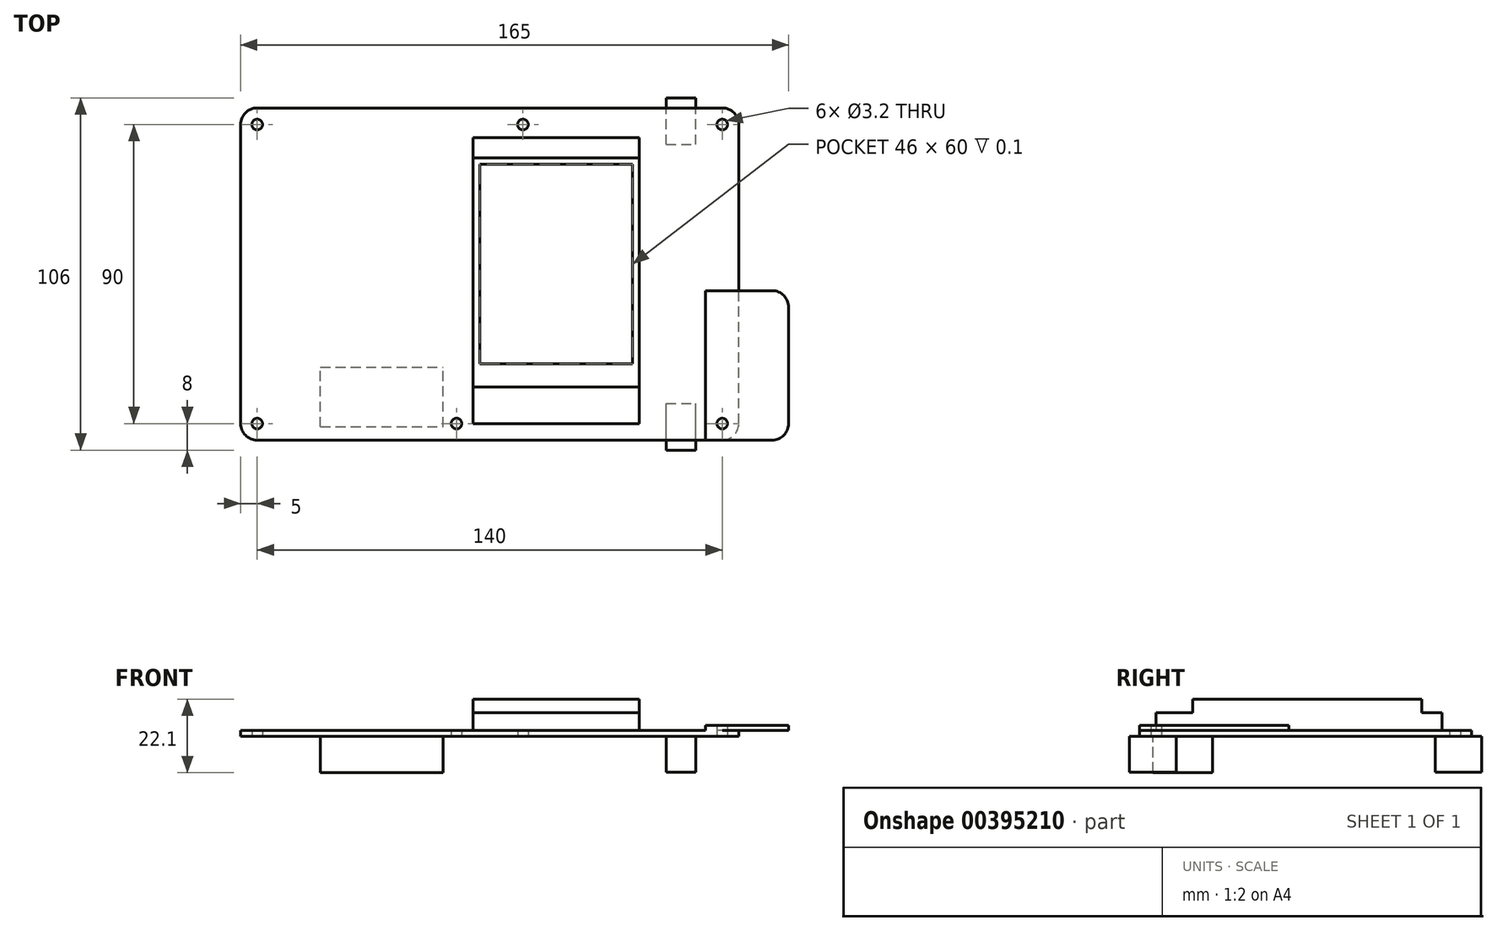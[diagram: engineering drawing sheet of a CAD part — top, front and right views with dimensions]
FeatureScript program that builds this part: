
annotation { "Feature Type Name" : "Feature", "Feature Type Description" : "" }
export const myFeature = defineFeature(function(context is Context, id is Id, definition is map)
    precondition{}
    {
        {
            var Q0;
            Q0=qCreatedBy(makeId("Top.planeOp"),FACE);
            var sketch = newSketch(context, id + "F0", { "sketchPlane" : qUnion([Q0])});
            skLineSegment(sketch, "E0.bottom", {"start": v(5, 0) * mm, "end": v(145, 0) * mm});
            skLineSegment(sketch, "E0.top", {"start": v(5, 100) * mm, "end": v(145, 100) * mm});
            skLineSegment(sketch, "E0.left", {"start": v(0, 5) * mm, "end": v(0, 95) * mm});
            skLineSegment(sketch, "E0.right", {"start": v(150, 5) * mm, "end": v(150, 95) * mm});
            skPoint(sketch, "E1.visualSharp", {"position": v(0, 100) * mm});
            skArc(sketch, "E1.filletArc", {"start": v(5, 100) * mm, "mid": v(1.46, 98.54) * mm, "end": v(0, 95) * mm});
            skPoint(sketch, "E2.visualSharp", {"position": v(150, 100) * mm});
            skArc(sketch, "E2.filletArc", {"start": v(150, 95) * mm, "mid": v(148.54, 98.54) * mm, "end": v(145, 100) * mm});
            skPoint(sketch, "E3.visualSharp", {"position": v(150, 0) * mm});
            skArc(sketch, "E3.filletArc", {"start": v(145, 0) * mm, "mid": v(148.54, 1.46) * mm, "end": v(150, 5) * mm});
            skPoint(sketch, "E4.visualSharp", {"position": v(0, 0) * mm});
            skArc(sketch, "E4.filletArc", {"start": v(0, 5) * mm, "mid": v(1.46, 1.46) * mm, "end": v(5, 0) * mm});
            skCircle(sketch, "E5", {"center": v(5, 95) * mm, "radius": 1.6 * mm});
            skCircle(sketch, "E6", {"center": v(5, 5) * mm, "radius": 1.6 * mm});
            skCircle(sketch, "E7", {"center": v(145, 5) * mm, "radius": 1.6 * mm});
            skCircle(sketch, "E8", {"center": v(145, 95) * mm, "radius": 1.6 * mm});
            skCircle(sketch, "E9", {"center": v(65, 5) * mm, "radius": 1.6 * mm});
            skCircle(sketch, "E10", {"center": v(85, 95) * mm, "radius": 1.6 * mm});
            skSolve(sketch);
        }
        {
            var Q0;
            Q0 = qSketchRegion(id + "F0", true);
            extrude(context, id + "F1", {"entities" : qUnion([Q0]), "depth" : 1.7 * mm});
        }
        {
            var Q0;
            Q0=makeQuery(id+"F1.opExtrude","CAP_FACE",FACE,{"disambiguationData":[OSD([sQuery(id+"F0.wireOp",EDGE,"E0.bottom"),sQuery(id+"F0.wireOp",EDGE,"E0.top"),sQuery(id+"F0.wireOp",EDGE,"E0.left"),sQuery(id+"F0.wireOp",EDGE,"E0.right"),sQuery(id+"F0.wireOp",EDGE,"E1.filletArc"),sQuery(id+"F0.wireOp",EDGE,"E2.filletArc"),sQuery(id+"F0.wireOp",EDGE,"E3.filletArc"),sQuery(id+"F0.wireOp",EDGE,"E4.filletArc"),sQuery(id+"F0.wireOp",EDGE,"E5"),sQuery(id+"F0.wireOp",EDGE,"E6"),sQuery(id+"F0.wireOp",EDGE,"E7"),sQuery(id+"F0.wireOp",EDGE,"E8"),sQuery(id+"F0.wireOp",EDGE,"E9"),sQuery(id+"F0.wireOp",EDGE,"E10")])],"isStart":false});
            var sketch = newSketch(context, id + "F2", { "sketchPlane" : qUnion([Q0])});
            skLineSegment(sketch, "E11.bottom", {"start": v(70, 91) * mm, "end": v(120, 91) * mm});
            skLineSegment(sketch, "E11.top", {"start": v(70, 5) * mm, "end": v(120, 5) * mm});
            skLineSegment(sketch, "E11.left", {"start": v(70, 91) * mm, "end": v(70, 5) * mm});
            skLineSegment(sketch, "E11.right", {"start": v(120, 91) * mm, "end": v(120, 5) * mm});
            skSolve(sketch);
        }
        {
            var Q0;
            Q0 = qSketchRegion(id + "F2", true);
            extrude(context, id + "F3", {"entities" : qUnion([Q0]), "operationType" : NewBodyOperationType.ADD, "depth" : 5.4 * mm});
        }
        {
            var Q0;
            Q0=makeQuery(id+"F3.opExtrude","CAP_FACE",FACE,{"disambiguationData":[OSD([sQuery(id+"F2.wireOp",EDGE,"E11.bottom"),sQuery(id+"F2.wireOp",EDGE,"E11.top"),sQuery(id+"F2.wireOp",EDGE,"E11.left"),sQuery(id+"F2.wireOp",EDGE,"E11.right")])],"isStart":false});
            var sketch = newSketch(context, id + "F4", { "sketchPlane" : qUnion([Q0])});
            skLineSegment(sketch, "E12.bottom", {"start": v(70, 85) * mm, "end": v(120, 85) * mm});
            skLineSegment(sketch, "E12.top", {"start": v(70, 16) * mm, "end": v(120, 16) * mm});
            skLineSegment(sketch, "E12.left", {"start": v(70, 85) * mm, "end": v(70, 16) * mm});
            skLineSegment(sketch, "E12.right", {"start": v(120, 85) * mm, "end": v(120, 16) * mm});
            skSolve(sketch);
        }
        {
            var Q0;
            Q0 = qSketchRegion(id + "F4", true);
            extrude(context, id + "F5", {"entities" : qUnion([Q0]), "operationType" : NewBodyOperationType.ADD, "depth" : 4 * mm});
        }
        {
            var Q0;
            Q0=makeQuery(id+"F5.opExtrude","CAP_FACE",FACE,{"disambiguationData":[OSD([sQuery(id+"F4.wireOp",EDGE,"E12.bottom"),sQuery(id+"F4.wireOp",EDGE,"E12.top"),sQuery(id+"F4.wireOp",EDGE,"E12.left"),sQuery(id+"F4.wireOp",EDGE,"E12.right")])],"isStart":false});
            var sketch = newSketch(context, id + "F6", { "sketchPlane" : qUnion([Q0])});
            skLineSegment(sketch, "E13.bottom", {"start": v(72, 83) * mm, "end": v(118, 83) * mm});
            skLineSegment(sketch, "E13.top", {"start": v(72, 23) * mm, "end": v(118, 23) * mm});
            skLineSegment(sketch, "E13.left", {"start": v(72, 83) * mm, "end": v(72, 23) * mm});
            skLineSegment(sketch, "E13.right", {"start": v(118, 83) * mm, "end": v(118, 23) * mm});
            skSolve(sketch);
        }
        {
            var Q0;
            Q0 = qSketchRegion(id + "F6", true);
            extrude(context, id + "F7", {"entities" : qUnion([Q0]), "operationType" : NewBodyOperationType.REMOVE, "oppositeDirection" : true, "depth" : .1 * mm});
        }
        {
            var Q0;
            Q0=makeQuery(id+"F1.opExtrude","CAP_FACE",FACE,{"disambiguationData":[OSD([sQuery(id+"F0.wireOp",EDGE,"E0.bottom"),sQuery(id+"F0.wireOp",EDGE,"E0.top"),sQuery(id+"F0.wireOp",EDGE,"E0.left"),sQuery(id+"F0.wireOp",EDGE,"E0.right"),sQuery(id+"F0.wireOp",EDGE,"E1.filletArc"),sQuery(id+"F0.wireOp",EDGE,"E2.filletArc"),sQuery(id+"F0.wireOp",EDGE,"E3.filletArc"),sQuery(id+"F0.wireOp",EDGE,"E4.filletArc"),sQuery(id+"F0.wireOp",EDGE,"E5"),sQuery(id+"F0.wireOp",EDGE,"E6"),sQuery(id+"F0.wireOp",EDGE,"E7"),sQuery(id+"F0.wireOp",EDGE,"E8"),sQuery(id+"F0.wireOp",EDGE,"E9"),sQuery(id+"F0.wireOp",EDGE,"E10")])],"isStart":false});
            var sketch = newSketch(context, id + "F8", { "sketchPlane" : qUnion([Q0])});
            skLineSegment(sketch, "E14.bottom", {"start": v(140, 0) * mm, "end": v(160, 0) * mm});
            skLineSegment(sketch, "E14.top", {"start": v(140, 45) * mm, "end": v(160, 45) * mm});
            skLineSegment(sketch, "E14.left", {"start": v(140, 0) * mm, "end": v(140, 45) * mm});
            skLineSegment(sketch, "E14.right", {"start": v(165, 5) * mm, "end": v(165, 40) * mm});
            skPoint(sketch, "E15.visualSharp", {"position": v(165, 45) * mm});
            skArc(sketch, "E15.filletArc", {"start": v(165, 40) * mm, "mid": v(163.54, 43.54) * mm, "end": v(160, 45) * mm});
            skPoint(sketch, "E16.visualSharp", {"position": v(165, 0) * mm});
            skArc(sketch, "E16.filletArc", {"start": v(160, 0) * mm, "mid": v(163.54, 1.46) * mm, "end": v(165, 5) * mm});
            skCircle(sketch, "E17.0", {"center": v(145, 5) * mm, "radius": 1.6 * mm});
            skSolve(sketch);
        }
        {
            var Q0;
            Q0 = qSketchRegion(id + "F8", true);
            extrude(context, id + "F9", {"entities" : qUnion([Q0]), "operationType" : NewBodyOperationType.ADD, "depth" : 1.6 * mm});
        }
        {
            var Q0;
            Q0=makeQuery(id+"F1.opExtrude","CAP_FACE",FACE,{"disambiguationData":[OSD([sQuery(id+"F0.wireOp",EDGE,"E0.bottom"),sQuery(id+"F0.wireOp",EDGE,"E0.top"),sQuery(id+"F0.wireOp",EDGE,"E0.left"),sQuery(id+"F0.wireOp",EDGE,"E0.right"),sQuery(id+"F0.wireOp",EDGE,"E1.filletArc"),sQuery(id+"F0.wireOp",EDGE,"E2.filletArc"),sQuery(id+"F0.wireOp",EDGE,"E3.filletArc"),sQuery(id+"F0.wireOp",EDGE,"E4.filletArc"),sQuery(id+"F0.wireOp",EDGE,"E5"),sQuery(id+"F0.wireOp",EDGE,"E6"),sQuery(id+"F0.wireOp",EDGE,"E7"),sQuery(id+"F0.wireOp",EDGE,"E8"),sQuery(id+"F0.wireOp",EDGE,"E9"),sQuery(id+"F0.wireOp",EDGE,"E10")])],"isStart":true});
            var sketch = newSketch(context, id + "F10", { "sketchPlane" : qUnion([Q0])});
            skLineSegment(sketch, "E18.bottom", {"start": v(24, -4) * mm, "end": v(61, -4) * mm});
            skLineSegment(sketch, "E18.top", {"start": v(24, -22) * mm, "end": v(61, -22) * mm});
            skLineSegment(sketch, "E18.left", {"start": v(24, -4) * mm, "end": v(24, -22) * mm});
            skLineSegment(sketch, "E18.right", {"start": v(61, -4) * mm, "end": v(61, -22) * mm});
            skSolve(sketch);
        }
        {
            var Q0;
            Q0 = qSketchRegion(id + "F10", true);
            extrude(context, id + "F11", {"entities" : qUnion([Q0]), "operationType" : NewBodyOperationType.ADD, "depth" : 11 * mm});
        }
        {
            var Q0;
            Q0=makeQuery(id+"F1.opExtrude","CAP_FACE",FACE,{"disambiguationData":[OSD([sQuery(id+"F0.wireOp",EDGE,"E0.bottom"),sQuery(id+"F0.wireOp",EDGE,"E0.top"),sQuery(id+"F0.wireOp",EDGE,"E0.left"),sQuery(id+"F0.wireOp",EDGE,"E0.right"),sQuery(id+"F0.wireOp",EDGE,"E1.filletArc"),sQuery(id+"F0.wireOp",EDGE,"E2.filletArc"),sQuery(id+"F0.wireOp",EDGE,"E3.filletArc"),sQuery(id+"F0.wireOp",EDGE,"E4.filletArc"),sQuery(id+"F0.wireOp",EDGE,"E5"),sQuery(id+"F0.wireOp",EDGE,"E6"),sQuery(id+"F0.wireOp",EDGE,"E7"),sQuery(id+"F0.wireOp",EDGE,"E8"),sQuery(id+"F0.wireOp",EDGE,"E9"),sQuery(id+"F0.wireOp",EDGE,"E10")])],"isStart":true});
            var sketch = newSketch(context, id + "F12", { "sketchPlane" : qUnion([Q0])});
            skLineSegment(sketch, "E19.bottom", {"start": v(128.1, -89) * mm, "end": v(137, -89) * mm});
            skLineSegment(sketch, "E19.top", {"start": v(128.1, -103) * mm, "end": v(137, -103) * mm});
            skLineSegment(sketch, "E19.left", {"start": v(128.1, -89) * mm, "end": v(128.1, -103) * mm});
            skLineSegment(sketch, "E19.right", {"start": v(137, -89) * mm, "end": v(137, -103) * mm});
            skLineSegment(sketch, "E20.bottom", {"start": v(128.1, 3) * mm, "end": v(137, 3) * mm});
            skLineSegment(sketch, "E20.top", {"start": v(128.1, -11) * mm, "end": v(137, -11) * mm});
            skLineSegment(sketch, "E20.left", {"start": v(128.1, 3) * mm, "end": v(128.1, -11) * mm});
            skLineSegment(sketch, "E20.right", {"start": v(137, 3) * mm, "end": v(137, -11) * mm});
            skSolve(sketch);
        }
        {
            var Q0;
            Q0 = qSketchRegion(id + "F12", true);
            extrude(context, id + "F13", {"entities" : qUnion([Q0]), "operationType" : NewBodyOperationType.ADD, "depth" : 10.8 * mm});
        }
    });
